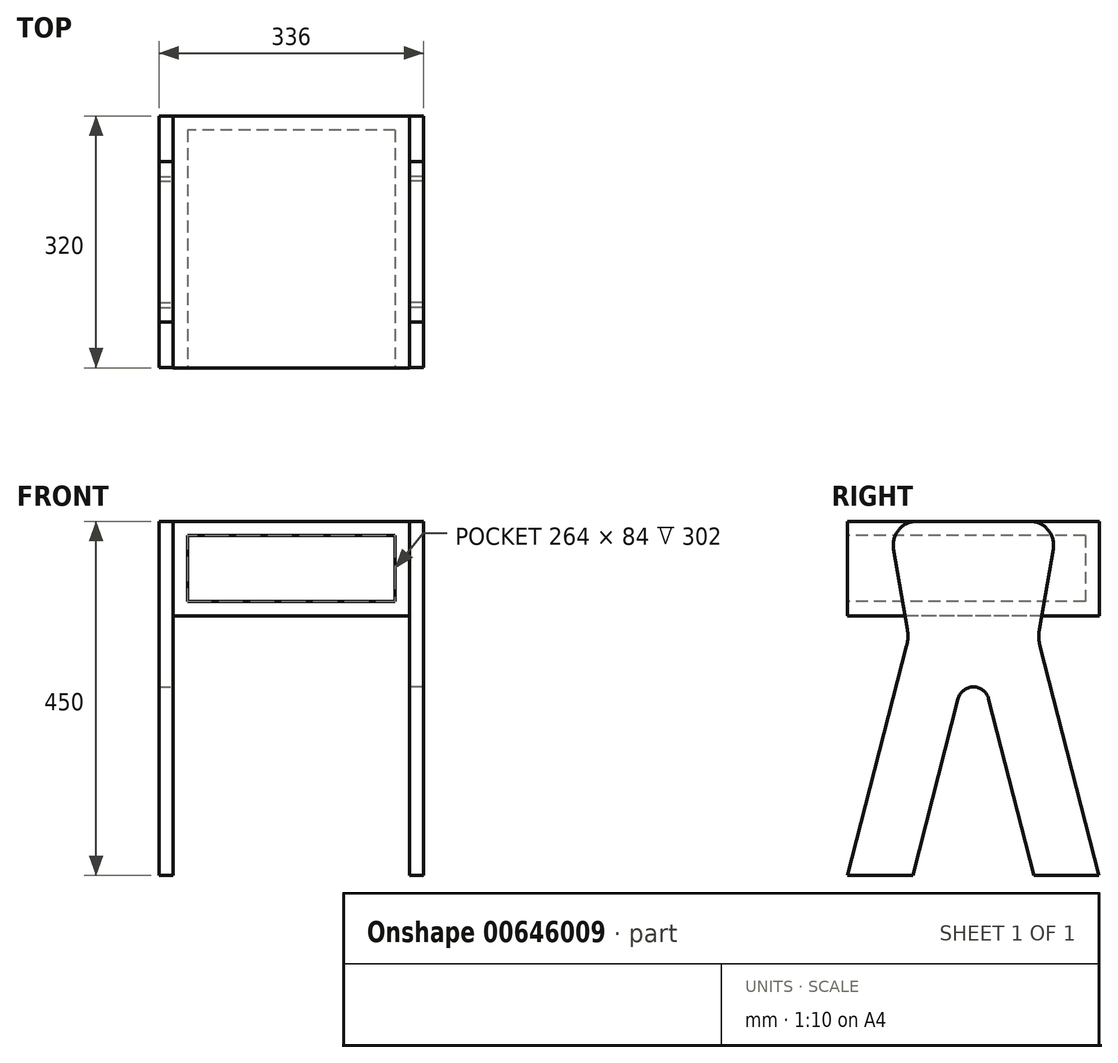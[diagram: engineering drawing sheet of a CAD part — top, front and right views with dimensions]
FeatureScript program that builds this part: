
annotation { "Feature Type Name" : "Feature", "Feature Type Description" : "" }
export const myFeature = defineFeature(function(context is Context, id is Id, definition is map)
    precondition{}
    {
        {
            var Q0;
            Q0=qCreatedBy(makeId("Right.planeOp"),FACE);
            cPlane(context, id + "F0", {"entities" : qUnion([Q0]), "cplaneType" : CPlaneType.OFFSET, "offset" : 150 * mm, "width" : 150 * mm, "height" : 150 * mm});
        }
        {
            var Q0;
            Q0=qCreatedBy(id+"F0.planeOp",FACE);
            var sketch = newSketch(context, id + "F1", { "sketchPlane" : qUnion([Q0])});
            skLineSegment(sketch, "E0.bottom", {"start": v(-71.8, 225) * mm, "end": v(71.8, 225) * mm});
            skLineSegment(sketch, "E0.top", {"start": v(-159.68, -225) * mm, "end": v(-77.08, -225) * mm});
            skPoint(sketch, "E0.middle", {"position": v(0, 0) * mm});
            skLineSegment(sketch, "E1", {"start": v(-77.08, -225) * mm, "end": v(-19.37, -0.39) * mm});
            skPoint(sketch, "E2.orphan", {"position": v(-175, 225) * mm});
            skPoint(sketch, "E0.right.end.orphan", {"position": v(175, -225) * mm});
            skPoint(sketch, "E3.orphan", {"position": v(-175, -225) * mm});
            skLineSegment(sketch, "E4.0", {"start": v(-159.68, -225) * mm, "end": v(-84.72, 66.73) * mm});
            skLineSegment(sketch, "E5", {"start": v(-101.38, 189.94) * mm, "end": v(-83.87, 87.6) * mm});
            skPoint(sketch, "E6.visualSharp", {"position": v(-82.06, 77.08) * mm});
            skArc(sketch, "E6.filletArc", {"start": v(-84.72, 66.73) * mm, "mid": v(-83.2, 77.13) * mm, "end": v(-83.87, 87.6) * mm});
            skPoint(sketch, "E7.visualSharp", {"position": v(-107.38, 225) * mm});
            skArc(sketch, "E7.filletArc", {"start": v(-71.8, 225) * mm, "mid": v(-94.74, 214.34) * mm, "end": v(-101.38, 189.94) * mm});
            skLineSegment(sketch, "E8", {"start": v(0, 75) * mm, "end": v(0, -37.17) * mm});
            skArc(sketch, "E9.MirrorCS", {"start": v(71.8, 225) * mm, "mid": v(94.74, 214.34) * mm, "end": v(101.38, 189.94) * mm});
            skLineSegment(sketch, "E10.MirrorCS", {"start": v(159.68, -225) * mm, "end": v(77.08, -225) * mm});
            skLineSegment(sketch, "E11.MirrorCS", {"start": v(101.38, 189.94) * mm, "end": v(83.87, 87.6) * mm});
            skArc(sketch, "E12.MirrorCS", {"start": v(84.72, 66.73) * mm, "mid": v(83.2, 77.13) * mm, "end": v(83.87, 87.6) * mm});
            skLineSegment(sketch, "E13.MirrorCS", {"start": v(77.08, -225) * mm, "end": v(19.37, -0.39) * mm});
            skLineSegment(sketch, "E14.MirrorCS", {"start": v(159.68, -225) * mm, "end": v(84.72, 66.73) * mm});
            skPoint(sketch, "E15.visualSharp", {"position": v(0, 75) * mm});
            skArc(sketch, "E15.filletArc", {"start": v(19.37, -0.39) * mm, "mid": v(0, 14.63) * mm, "end": v(-19.37, -0.39) * mm});
            skPoint(sketch, "E16.orphan", {"position": v(175, 225) * mm});
            skSolve(sketch);
        }
        {
            var Q0;
            Q0 = qSketchRegion(id + "F1", true);
            extrude(context, id + "F2", {"entities" : qUnion([Q0]), "depth" : 18 * mm, "offsetDistance" : 25 * mm});
        }
        {
            var Q0;
            Q0=qCreatedBy(makeId("Right.planeOp"),FACE);
            var sketch = newSketch(context, id + "F3", { "sketchPlane" : qUnion([Q0])});
            skLineSegment(sketch, "E17", {"start": v(160, 225) * mm, "end": v(160, 105) * mm});
            skLineSegment(sketch, "E18", {"start": v(160, 105) * mm, "end": v(-160, 105) * mm});
            skLineSegment(sketch, "E19", {"start": v(-160, 105) * mm, "end": v(-160, 225) * mm});
            skPoint(sketch, "E20.0.8.end.orphan", {"position": v(101.38, 189.94) * mm});
            skPoint(sketch, "E21.orphan", {"position": v(-101.38, 189.94) * mm});
            skLineSegment(sketch, "E22", {"start": v(160, 225) * mm, "end": v(-160, 225) * mm});
            skSolve(sketch);
        }
        {
            var Q0;
            Q0 = qSketchRegion(id + "F3", true);
            extrude(context, id + "F4", {"entities" : qUnion([Q0]), "endBound" : BoundingType.SYMMETRIC, "depth" : 300 * mm, "offsetDistance" : 25 * mm});
        }
        {
            var Q0;
            Q0=makeQuery(id+"F2.opExtrude","SWEPT_BODY",BODY,{"disambiguationData":[OSD([sQuery(id+"F1.wireOp",EDGE,"E0.bottom"),sQuery(id+"F1.wireOp",EDGE,"E0.top"),sQuery(id+"F1.wireOp",EDGE,"E1"),sQuery(id+"F1.wireOp",EDGE,"E4.0"),sQuery(id+"F1.wireOp",EDGE,"E5"),sQuery(id+"F1.wireOp",EDGE,"E6.filletArc"),sQuery(id+"F1.wireOp",EDGE,"E7.filletArc"),sQuery(id+"F1.wireOp",EDGE,"E9.MirrorCS"),sQuery(id+"F1.wireOp",EDGE,"E10.MirrorCS"),sQuery(id+"F1.wireOp",EDGE,"E11.MirrorCS"),sQuery(id+"F1.wireOp",EDGE,"E12.MirrorCS"),sQuery(id+"F1.wireOp",EDGE,"E13.MirrorCS"),sQuery(id+"F1.wireOp",EDGE,"E14.MirrorCS"),sQuery(id+"F1.wireOp",EDGE,"E15.filletArc")])]});
            var Q1;
            Q1=qCreatedBy(makeId("Right.planeOp"),FACE);
            mirror(context, id + "F5", {"entities" : qUnion([Q0]), "mirrorPlane" : qUnion([Q1])});
        }
        {
            var Q0;
            Q0=makeQuery(id+"F4.opExtrude","SWEPT_FACE",FACE,{"disambiguationData":[OSD([sQuery(id+"F3.wireOp",EDGE,"E19")])]});
            shell(context, id + "F6", {"entities" : qUnion([Q0]), "thickness" : 18 * mm});
        }
    });
